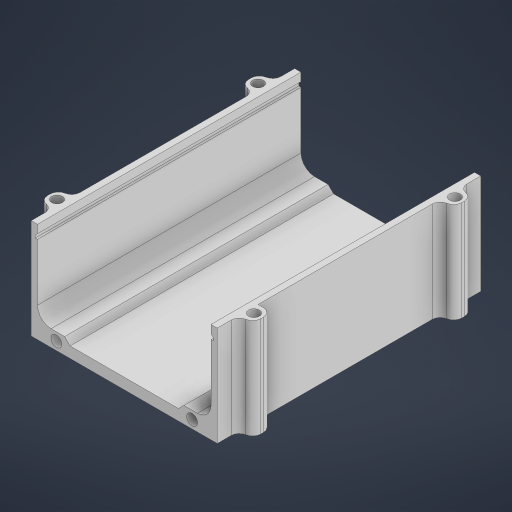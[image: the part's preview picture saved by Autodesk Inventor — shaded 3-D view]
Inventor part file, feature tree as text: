
AUTODESK INVENTOR PART (.ipt)
format: ipt  version: 2023 (Build 270158000, 158)  size: 335,360 bytes
history: native  units: mm
features: sketch x6, extrude x4, fillet x4, hole x2, chamfer x2, projected_geometry x2, mirror x1, pattern_linear x1
ambient origin geometry x8: Origin, YZ Plane, XZ Plane, XY Plane, X Axis, Y Axis, Z Axis, Center Point
bodies: Solid1 (feature_tree)
feature tree (22):
  extrude  "Extrusion1"  Depth=0.8mm
  extrude  "Extrusion3"  Depth=1.5mm
  fillet  "Fillet2"  Radius=1.5mm
  hole  "Hole1"  [1 undecoded]
  mirror  "Mirror1"
  fillet  "Fillet3"  Radius=2.2mm
  fillet  "Fillet4"  [1 undecoded]
  chamfer  "Chamfer2"  Distance=50.0mm
  extrude  "Extrusion4"  Depth=2.0mm
  chamfer  "Chamfer3"  Distance=8.0mm
  hole  "Hole2"  [1 undecoded]
  extrude  "Extrusion2"  Depth=2.0mm
  fillet  "Fillet1"  Radius=8.0mm
  pattern_linear  "Rectangular Pattern1"  Spacing1=97.0mm  [1 undecoded]
  sketch  "Sketch1"  dims[d0=6.0mm d2=0.8mm]
  sketch  "Sketch2"  dims[d3=3.0mm d4=1.8mm d5=1.5mm]
  projected_geometry  "Projected Loop1"
  sketch  "Sketch5"  dims[d9=26.0mm d10=97.0mm d11=0.0mm d12=2.2mm d13=0.0mm d14=0.0mm]
  sketch  "Sketch6"  dims[d15=65.5mm]
  projected_geometry  "Projected Loop4"
  sketch  "Sketch7"  dims[d19=4.0mm d20=50.0mm d22=18.0mm]
  sketch  "Sketch8"  dims[d23=5.0mm d24=7.0mm d25=8.0mm d26=5.0mm d27=7.0mm d28=8.0mm d29=97.0mm d30=0.0mm d31=3.0mm d32=4.0mm d33=6.0mm d34=4.0mm d35=2.0mm d36=90.0deg d37=8.0mm d38=20.594885mm d39=5.0mm d40=3.0mm d41=0.8mm d42=2.0mm d43=45.0deg d44=2.0mm d45=6.0mm d46=6.0mm d47=0.0mm d48=0.0mm d49=1.0mm d50=2.0mm d51=45.0deg d52=50.0mm d53=25.0mm d54=3.0mm d55=4.0mm d56=6.0mm d57=4.0mm d58=2.0mm d59=90.0deg d60=8.0mm d61=20.594885mm]
note: 4 required parameter values undecoded (feature->parameter linkage not recoverable at this tier; creation-order binding heuristic only, values carry confidence <= 0.55)
